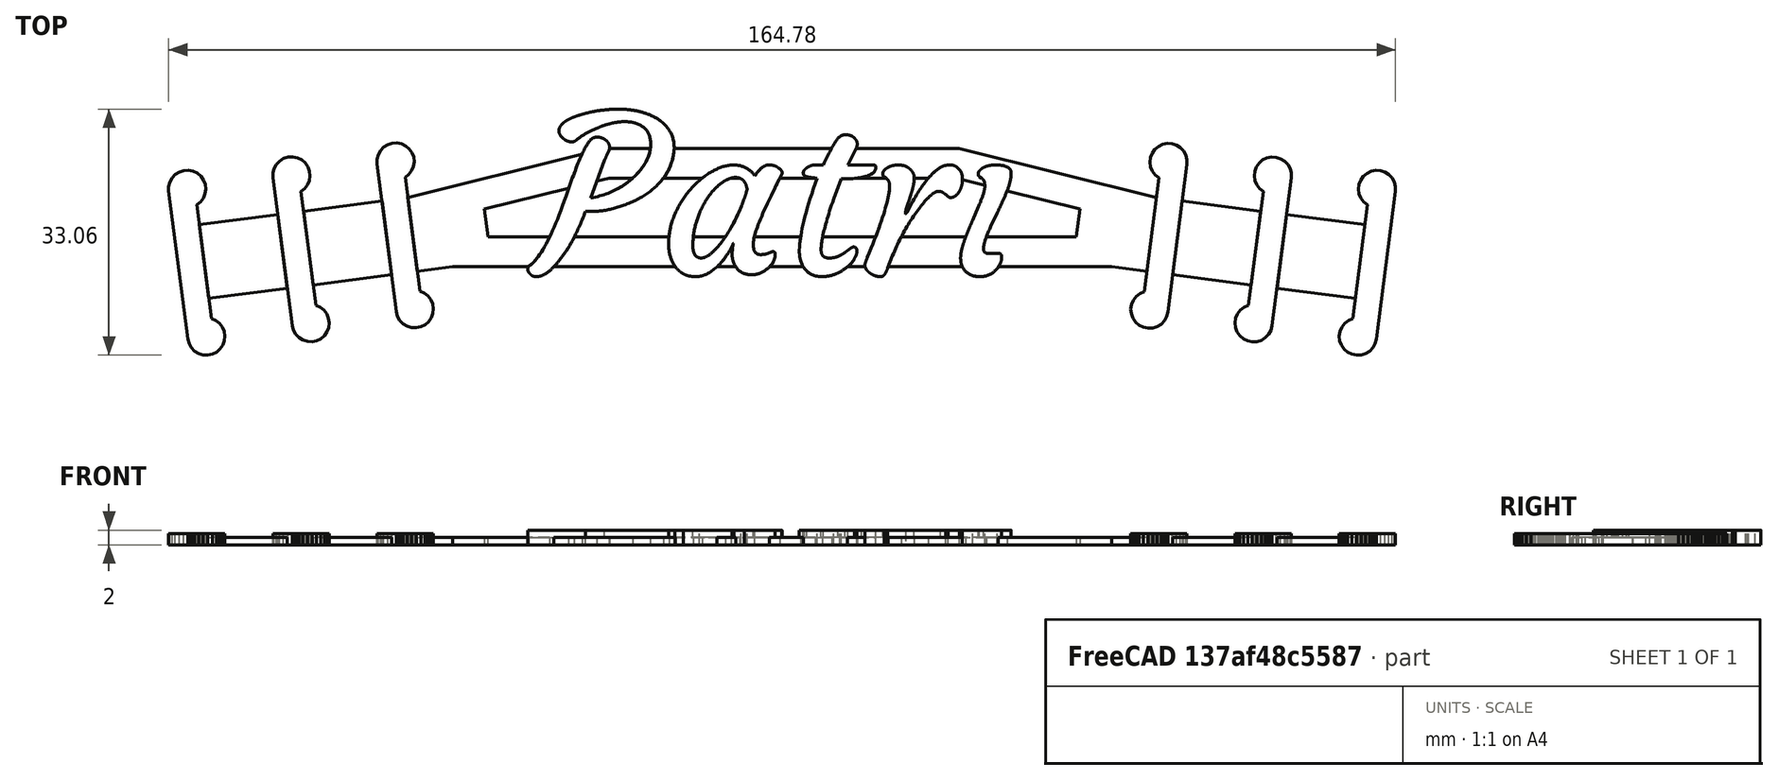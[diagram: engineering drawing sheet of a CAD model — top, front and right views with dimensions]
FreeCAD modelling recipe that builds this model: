
FCSTD DOCUMENT  (FreeCAD 0.18R4 (GitTag))
Label: ear_saver_martin
License: All rights reserved
LicenseURL: http://en.wikipedia.org/wiki/All_rights_reserved
objects: Part::Feature×1, Part::Part2DObjectPython×1, Part::Extrusion×1, Part::Box×1, Part::Cut×1, Part::MultiFuse×1, Mesh::Feature×1
note: 6 computed .brp shape members not serialized (recipe doc carries the construction recipe); baked Part::Feature solids carry a one-line shape summary decoded from their .brp

FEATURE [Part::Feature] ear_saver001_solid001  label="ear_saver001 (Solid)001"
  shape: bbox 164.8 x 28.52 x 1.5 mm, 279 faces (baked)
FEATURE [Part::Part2DObjectPython] ShapeString  # Draft 2D object (typed FeaturePython)
  FontFile = <userpath>/Documents/fonts/Courgette-Regular.ttf
  Placement = pos=(-20.38,14.74,0) rot=(0,0,1;0rad)
  Size = 25
  String = Patri
  Tracking = 0
FEATURE [Part::Extrusion] Extrude001
  Base = -> ShapeString
  Dir = (0,0,1)
  DirMode = 2
  FaceMakerClass = Part::FaceMakerBullseye
  LengthFwd = 2
  LengthRev = 0
  Placement = pos=(-16,-29,0) rot=(0,0,1;0rad)
  Solid = true
  Symmetric = false
FEATURE [Part::Box] Box  label="Cube"
  AttacherType = Attacher::AttachEngine3D
  Height = 10
  Length = 10
  Placement = pos=(24,3,-1) rot=(0,0,1;0rad)
  Width = 10
FEATURE [Part::Cut] Cut
  Base = -> Extrude001
  Tool = -> Box
FEATURE [Part::MultiFuse] Fusion
  Shapes = -> [Cut,ear_saver001_solid001]
FEATURE [Mesh::Feature] Mesh  label="Fusion (Meshed)"
